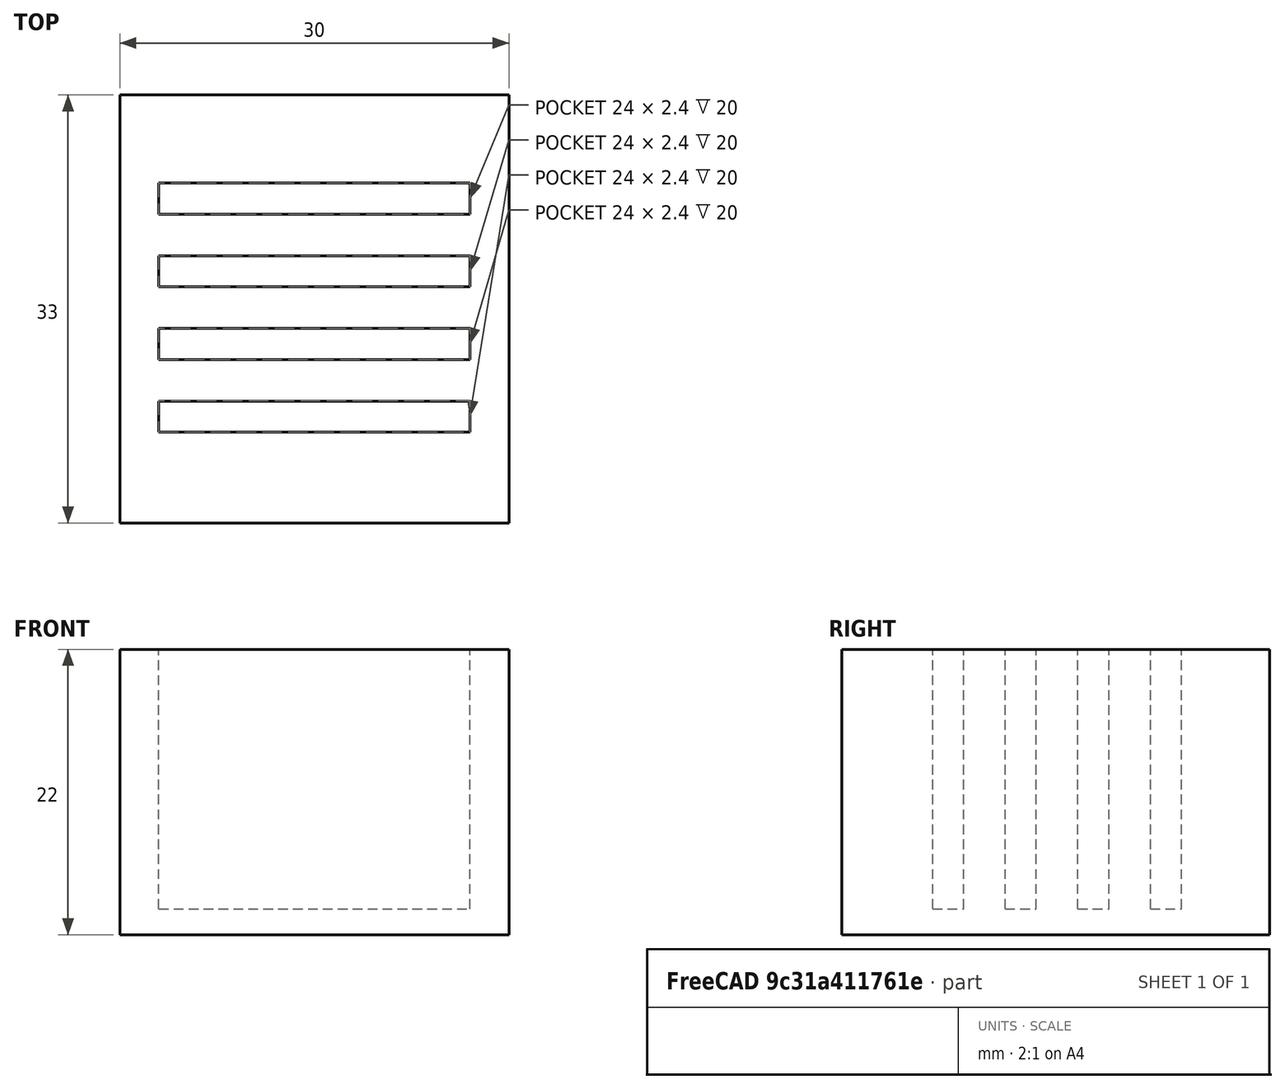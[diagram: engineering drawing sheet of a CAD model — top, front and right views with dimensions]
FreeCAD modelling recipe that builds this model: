
FCSTD DOCUMENT  (FreeCAD 0.16R6707 (Git))
Label: Porta_SD
License: CreativeCommons Attribution-ShareAlike
LicenseURL: http://creativecommons.org/licenses/by-sa/4.0/
objects: Part::Box×5, Part::MultiFuse×1, Part::Cut×1
note: 7 computed .brp shape members not serialized (recipe doc carries the construction recipe); baked Part::Feature solids carry a one-line shape summary decoded from their .brp

FEATURE [Part::Box] Box  label="Base"
  Height = 22
  Length = 30
  Width = 33
FEATURE [Part::Box] Box001  label="Ranura-1"
  Height = 20
  Length = 24
  Width = 2.4
FEATURE [Part::Box] Box002  label="Ranura-002"
  Height = 20
  Length = 24
  Placement = pos=(0,5.6,0) rot=(0,0,1;0rad)
  Width = 2.4
FEATURE [Part::Box] Box003  label="Ranura-003"
  Height = 20
  Length = 24
  Placement = pos=(0,11.2,0) rot=(0,0,1;0rad)
  Width = 2.4
FEATURE [Part::Box] Box004  label="Ranura-004"
  Height = 20
  Length = 24
  Placement = pos=(0,16.8,0) rot=(0,0,1;0rad)
  Width = 2.4
FEATURE [Part::MultiFuse] Fusion  label="Ranuras"
  Placement = pos=(3,7,2) rot=(0,0,1;0rad)
  Shapes = -> [Box001,Box002,Box003,Box004]
FEATURE [Part::Cut] Cut  label="Porta_SD"
  Base = -> Box
  Tool = -> Fusion
